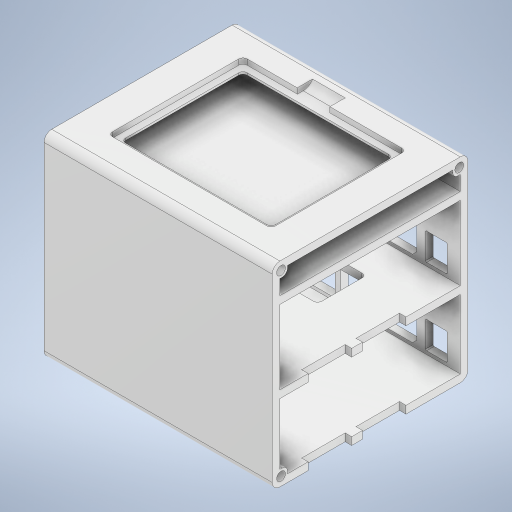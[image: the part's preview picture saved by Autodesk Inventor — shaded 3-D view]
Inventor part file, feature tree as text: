
AUTODESK INVENTOR PART (.ipt)
format: ipt  version: 2024 (Build 280153000, 153)  size: 709,632 bytes
history: native  units: mm
features: extrude x14, sketch x14, fillet x11, chamfer x2
ambient origin geometry x8: Origin, YZ Plane, XZ Plane, XY Plane, X Axis, Y Axis, Z Axis, Center Point
bodies: Solid1 (feature_tree)
feature tree (41):
  extrude  "Extrusion1"  Depth=90.0mm
  extrude  "Extrusion2"  Depth=3.5mm
  fillet  "Fillet1"  Radius=3.5mm
  fillet  "Fillet2"  Radius=3.5mm
  extrude  "Extrusion3"  Depth=7.0mm
  extrude  "Extrusion4"  Depth=7.0mm
  extrude  "Extrusion5"  Depth=7.0mm
  extrude  "Extrusion6"  Depth=3.49579mm
  extrude  "Extrusion7"  Depth=3.5mm
  fillet  "Fillet3"  Radius=34.0mm
  fillet  "Fillet4"  Radius=3.5mm
  chamfer  "Chamfer1"  Distance=105.0mm
  fillet  "Fillet5"  Radius=2.5mm
  extrude  "Extrusion9"  Depth=4.0mm
  extrude  "Extrusion11"  Depth=4.0mm
  extrude  "Extrusion12"  Depth=25.0mm
  fillet  "Fillet12"  Radius=20.0mm
  extrude  "Extrusion13"  Depth=20.0mm
  extrude  "Extrusion14"  Depth=3.0mm
  fillet  "Fillet13"  Radius=10.0mm
  extrude  "Extrusion15"  Depth=32.5mm
  fillet  "Fillet14"  Radius=3.0mm
  sketch  "Sketch1"  dims[d0=90.0mm d1=90.0mm]
  sketch  "Sketch2"  dims[d2=105.0mm d3=0.0mm d4=3.5mm d5=3.5mm d6=3.5mm]
  sketch  "Sketch4"  dims[d7=3.5mm d8=7.0mm]
  sketch  "Sketch5"  dims[d10=7.0mm d11=7.0mm]
  sketch  "Sketch6"  dims[d12=7.0mm d13=7.0mm]
  sketch  "Sketch7"  dims[d15=3.5mm d16=3.49579mm]
  sketch  "Sketch8"  dims[d17=31.694mm d18=3.5mm d19=34.0mm d20=3.5mm d21=105.0mm d22=0.0mm d23=2.5mm]
  sketch  "Sketch10"  dims[d24=3.5mm d28=4.0mm]
  sketch  "Sketch12"  dims[d40=0.0mm d41=0.0mm d42=25.0mm d43=20.0mm]
  sketch  "Sketch13"  dims[d44=5.0mm d45=20.0mm]
  sketch  "Sketch14"  dims[d46=3.0mm d47=3.0mm d48=10.0mm d49=0.0mm]
  sketch  "Sketch15"  dims[d50=47.5mm d51=32.5mm d52=3.0mm d53=10.0mm d54=0.0mm d55=5.0mm d56=10.0mm]
  sketch  "Sketch16"  dims[d57=3.0mm d58=10.0mm d59=0.0mm d60=3.0mm d68=18.0mm d69=21.0mm d70=4.0mm d71=10.0mm d72=14.0mm d73=10.0mm d74=0.0mm d75=2.0mm d76=5.0mm d77=2.0mm d78=16.0mm d79=3.0mm d80=18.0mm d81=1.5mm d82=31.0mm d83=14.0mm d84=2.5mm d85=0.5mm d86=0.5mm d87=2.0mm d88=2.0mm d89=45.0deg d90=0.5mm d116=15.0mm d117=14.0mm d118=8.0mm d119=10.0mm d120=0.0mm d121=2.5mm d122=14.0mm d123=1.5mm d124=31.0mm d125=18.0mm d126=3.0mm d127=16.0mm d128=2.0mm d129=5.0mm d130=10.0mm d131=14.0mm d132=4.0mm d133=18.0mm d134=21.0mm d135=2.0mm d136=3.0mm d138=0.0mm d139=10.0mm d140=0.5mm d141=0.5mm d142=45.0deg d143=2.0mm d144=2.0mm d145=0.5mm d146=73.0mm d147=2.5mm d148=1.0mm d150=1.0mm d151=1.0mm d152=5.0mm d153=0.0mm d154=15.0mm d155=40.0mm d156=90.0deg d157=15.0mm d158=12.5mm d159=90.0deg d160=20.0mm d161=5.0mm d162=0.0mm d163=2.0mm d166=15.0mm d167=10.0mm d168=15.0mm d169=10.0mm d170=3.0mm d171=3.0mm d172=3.0mm d173=3.0mm d174=10.0mm d175=0.0mm d176=3.0mm d177=90.0deg d178=3.0mm d179=3.0mm d180=3.0mm d181=2.5mm d182=0.0mm d183=2.0mm d184=30.5mm d185=7.5mm d186=7.0mm d187=15.0mm d188=2.5mm d189=0.0mm d190=5.0mm d25=0.0mm d26=0.0mm d27=0.0mm]
  fillet  "Fillet9"  Radius=10.0mm
  fillet  "Fillet10"  Radius=5.0mm
  fillet  "Fillet11"  Radius=10.0mm
  sketch  "Sketch11"  dims[d32=4.0mm d35=4.0mm]
  chamfer  "Chamfer3"  Distance=10.0mm
  extrude  "Extrusion10"  Depth=3.0mm
